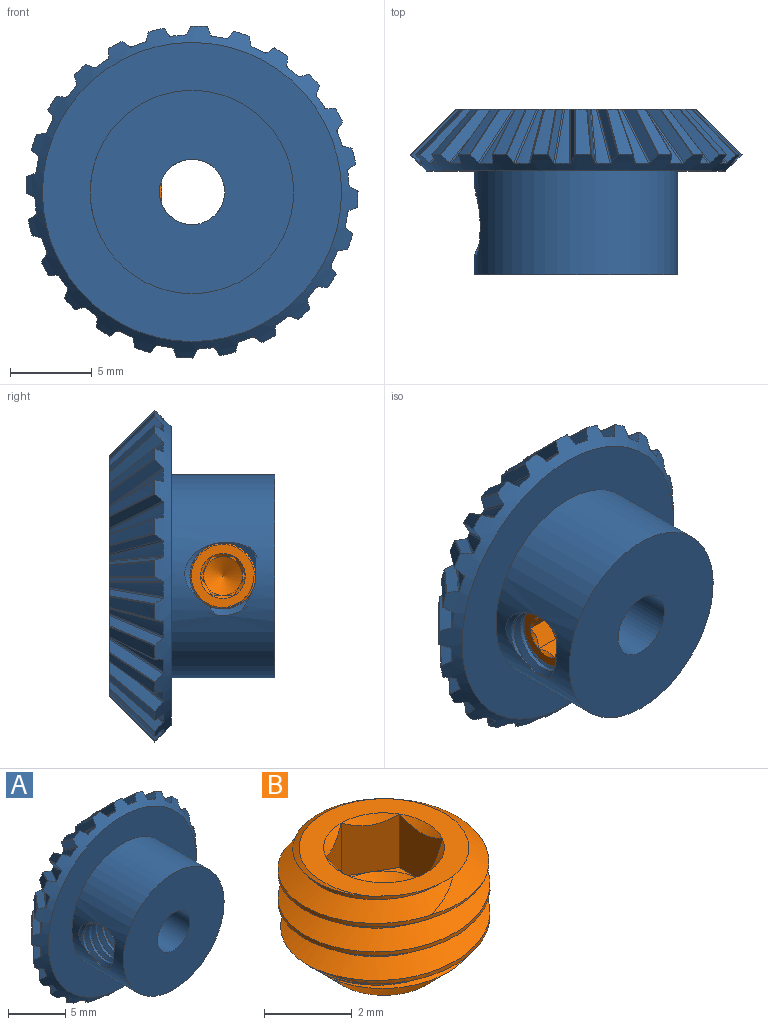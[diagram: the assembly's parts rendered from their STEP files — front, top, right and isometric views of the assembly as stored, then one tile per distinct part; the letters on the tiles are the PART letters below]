
ASSEMBLY  parts=2 mates=1
PART A: 224 faces, bbox 20.3x10.2x20.3 mm
  f0: cylinder r=2.41mm len=4.83mm, axis (-1,0,0), area 8.2mm2, adj f8,f9,f220,f221,f222,f223
  f1: cylinder r=2.41mm len=3.92mm, axis (-1,0,0), area 0.4mm2, adj f8,f218,f219
  f2: cylinder r=2.41mm len=2.98mm, axis (-1,0,0), area 0.3mm2, adj f8,f212,f213,f214
  f3: cone r=10.16mm half-angle=45deg, axis (0,-1,0), area 3.1mm2, adj f4,f14,f15,f18
  f4: cone r=10.16mm half-angle=45deg, axis (0,1,0), area 61.8mm2, adj f3,f13,f15,f16,f17,f18,f19,f20
  f5: cylinder r=2.02mm len=0.81mm, axis (-1,0,0), area 0.2mm2, adj f8,f208,f213
  f6: cylinder r=2.02mm len=4.59mm, axis (-1,0,0), area 16.9mm2, adj f8,f9,f218,f220,f222
  f7: cylinder r=2.02mm len=2.26mm, axis (-1,0,0), area 0.5mm2, adj f8,f212,f219
  f8: cylinder r=2mm len=10.13mm, axis (0,-1,0), area 107.9mm2, adj f0,f1,f2,f5,f6,f7,f10,f11
  f9: cylinder r=6.22mm len=12.45mm, axis (0,1,0), area 233.2mm2, adj f0,f6,f12,f13,f206,f220,f221,f222
  f10: cylinder r=2.02mm len=1.49mm, axis (-1,0,0), area 0.3mm2, adj f8,f211,f216
  f11: cylinder r=2.02mm len=3.04mm, axis (-1,0,0), area 0.7mm2, adj f8,f215,f223
  f12: cylinder r=2.02mm len=1.27mm, axis (-1,0,0), area 0mm2, adj f9,f221
  f13: plane 18.31x18.31mm, normal (0,-1,0), area 141.7mm2, adj f4,f9
  f14: plane 14.79x14.79mm, normal (0,1,0), area 137.6mm2, adj f3,f8,f15,f16,f17,f18,f19,f20
  f15: cylinder r=0.05mm len=2.83mm, axis (0,-0.71,-0.71), area 0.2mm2, adj f3,f4,f14,f16
  f16: plane 3.76x3.28mm, normal (0.94,0.24,-0.24), area 3.1mm2, adj f4,f14,f15,f17
  f17: cylinder r=0.1mm len=3.37mm, axis (0,-0.71,-0.71), area 0.6mm2, adj f4,f14,f16,f19
  f18: cylinder r=0.05mm len=2.83mm, axis (0.06,0.71,0.7), area 0.2mm2, adj f3,f4,f14,f20
  f19: cone r=5.83mm half-angle=45deg, axis (0,-1,0), area 2.7mm2, adj f4,f14,f17,f21
  f20: plane 3.77x3.28mm, normal (-0.96,0.24,-0.16), area 3.1mm2, adj f4,f14,f18,f22
  f21: cylinder r=0.1mm len=3.37mm, axis (-0.12,0.71,0.7), area 0.6mm2, adj f4,f14,f19,f23
  f22: cylinder r=0.1mm len=3.37mm, axis (0.06,0.71,0.7), area 0.6mm2, adj f4,f14,f20,f24
  f23: plane 3.66x3.28mm, normal (-0.88,0.24,-0.4), area 3.1mm2, adj f4,f14,f21,f25
  f24: cone r=5.83mm half-angle=45deg, axis (0,-1,0), area 2.7mm2, adj f4,f14,f22,f26
  f25: cylinder r=0.05mm len=2.83mm, axis (-0.12,0.71,0.7), area 0.2mm2, adj f4,f14,f23,f27
  f26: cylinder r=0.1mm len=3.37mm, axis (-0.18,-0.71,-0.68), area 0.6mm2, adj f4,f14,f24,f28
  f27: cone r=10.16mm half-angle=45deg, axis (0,-1,0), area 3.1mm2, adj f4,f14,f25,f29
  f28: plane 3.57x3.28mm, normal (0.85,0.24,-0.48), area 3.1mm2, adj f4,f14,f26,f30
  f29: cylinder r=0.05mm len=2.83mm, axis (0.18,-0.71,-0.68), area 0.2mm2, adj f4,f14,f27,f31
  f30: cylinder r=0.05mm len=2.83mm, axis (-0.18,-0.71,-0.68), area 0.2mm2, adj f4,f14,f28,f32
  f31: plane 3.69x3.28mm, normal (0.97,0.24,0.01), area 3.1mm2, adj f4,f14,f29,f33
  f32: cone r=10.16mm half-angle=45deg, axis (0,-1,0), area 3.1mm2, adj f4,f14,f30,f34
  f33: cylinder r=0.1mm len=3.37mm, axis (0.18,-0.71,-0.68), area 0.6mm2, adj f4,f14,f31,f35
  f34: cylinder r=0.05mm len=2.83mm, axis (0.24,0.71,0.66), area 0.2mm2, adj f4,f14,f32,f36
  f35: cone r=5.83mm half-angle=45deg, axis (0,-1,0), area 2.7mm2, adj f4,f14,f33,f37
  f36: plane 3.62x3.28mm, normal (-0.97,0.24,0.09), area 3.1mm2, adj f4,f14,f34,f38
  f37: cylinder r=0.1mm len=3.37mm, axis (-0.3,0.71,0.64), area 0.6mm2, adj f4,f14,f35,f39
  f38: cylinder r=0.1mm len=3.37mm, axis (0.24,0.71,0.66), area 0.6mm2, adj f4,f14,f36,f40
  f39: plane 3.3x3.28mm, normal (-0.75,0.24,-0.62), area 3.1mm2, adj f4,f14,f37,f41
  f40: cone r=5.83mm half-angle=45deg, axis (0,-1,0), area 2.7mm2, adj f4,f14,f38,f42
  f41: cylinder r=0.05mm len=2.83mm, axis (-0.3,0.71,0.64), area 0.2mm2, adj f4,f14,f39,f43
  f42: cylinder r=0.1mm len=3.37mm, axis (-0.35,-0.71,-0.61), area 0.6mm2, adj f4,f14,f40,f44
  f43: cone r=10.16mm half-angle=45deg, axis (0,-1,0), area 3.1mm2, adj f4,f14,f41,f45
  f44: plane 3.28x3.13mm, normal (0.69,0.24,-0.68), area 3.1mm2, adj f4,f14,f42,f46
  f45: cylinder r=0.05mm len=2.83mm, axis (0.35,-0.71,-0.61), area 0.2mm2, adj f4,f14,f43,f47
  f46: cylinder r=0.05mm len=2.83mm, axis (-0.35,-0.71,-0.61), area 0.2mm2, adj f4,f14,f44,f48
  f47: plane 3.38x3.28mm, normal (0.93,0.24,0.26), area 3.1mm2, adj f4,f14,f45,f49
  f48: cone r=10.16mm half-angle=45deg, axis (0,-1,0), area 3.1mm2, adj f4,f14,f46,f50
  f49: cylinder r=0.1mm len=3.37mm, axis (0.35,-0.71,-0.61), area 0.6mm2, adj f4,f14,f47,f51
  f50: cylinder r=0.05mm len=2.83mm, axis (0.41,0.71,0.58), area 0.2mm2, adj f4,f14,f48,f52
  f51: cone r=5.83mm half-angle=45deg, axis (0,-1,0), area 2.7mm2, adj f4,f14,f49,f53
  f52: plane 3.28x3.22mm, normal (-0.91,0.24,0.34), area 3.1mm2, adj f4,f14,f50,f54
  f53: cylinder r=0.1mm len=3.37mm, axis (-0.45,0.71,0.54), area 0.6mm2, adj f4,f14,f51,f55
  f54: cylinder r=0.1mm len=3.37mm, axis (0.41,0.71,0.58), area 0.6mm2, adj f4,f14,f52,f56
  f55: plane 3.28x2.72mm, normal (-0.56,0.24,-0.79), area 3.1mm2, adj f4,f14,f53,f57
  f56: cone r=5.83mm half-angle=45deg, axis (0,-1,0), area 2.7mm2, adj f4,f14,f54,f58
  f57: cylinder r=0.05mm len=2.83mm, axis (-0.45,0.71,0.54), area 0.2mm2, adj f4,f14,f55,f59
  f58: cylinder r=0.1mm len=3.37mm, axis (-0.5,-0.71,-0.5), area 0.6mm2, adj f4,f14,f56,f60
  f59: cone r=10.16mm half-angle=45deg, axis (0,-1,0), area 3.1mm2, adj f4,f14,f57,f61
  f60: plane 3.28x2.83mm, normal (0.49,0.24,-0.84), area 3.1mm2, adj f4,f14,f58,f62
  f61: cylinder r=0.05mm len=2.83mm, axis (0.5,-0.71,-0.5), area 0.2mm2, adj f4,f14,f59,f63
  f62: cylinder r=0.05mm len=2.83mm, axis (-0.5,-0.71,-0.5), area 0.2mm2, adj f4,f14,f60,f64
  f63: plane 3.28x2.83mm, normal (0.84,0.24,0.49), area 3.1mm2, adj f4,f14,f61,f65
  f64: cone r=10.16mm half-angle=45deg, axis (0,-1,0), area 3.1mm2, adj f4,f14,f62,f66
  f65: cylinder r=0.1mm len=3.37mm, axis (0.5,-0.71,-0.5), area 0.6mm2, adj f4,f14,f63,f67
  f66: cylinder r=0.05mm len=2.83mm, axis (0.54,0.71,0.45), area 0.2mm2, adj f4,f14,f64,f68
  f67: cone r=5.83mm half-angle=45deg, axis (0,-1,0), area 2.7mm2, adj f4,f14,f65,f69
  f68: plane 3.28x2.72mm, normal (-0.79,0.24,0.56), area 3.1mm2, adj f4,f14,f66,f70
  f69: cylinder r=0.1mm len=3.37mm, axis (-0.58,0.71,0.41), area 0.6mm2, adj f4,f14,f67,f71
  f70: cylinder r=0.1mm len=3.37mm, axis (0.54,0.71,0.45), area 0.6mm2, adj f4,f14,f68,f72
  f71: plane 3.28x3.22mm, normal (-0.34,0.24,-0.91), area 3.1mm2, adj f4,f14,f69,f73
  f72: cone r=5.83mm half-angle=45deg, axis (0,-1,0), area 2.7mm2, adj f4,f14,f70,f74
  f73: cylinder r=0.05mm len=2.83mm, axis (-0.58,0.71,0.41), area 0.2mm2, adj f4,f14,f71,f75
  f74: cylinder r=0.1mm len=3.37mm, axis (-0.61,-0.71,-0.35), area 0.6mm2, adj f4,f14,f72,f76
  f75: cone r=10.16mm half-angle=45deg, axis (0,-1,0), area 3.1mm2, adj f4,f14,f73,f77
  f76: plane 3.38x3.28mm, normal (0.26,0.24,-0.93), area 3.1mm2, adj f4,f14,f74,f78
  f77: cylinder r=0.05mm len=2.83mm, axis (0.61,-0.71,-0.35), area 0.2mm2, adj f4,f14,f75,f79
  f78: cylinder r=0.05mm len=2.83mm, axis (-0.61,-0.71,-0.35), area 0.2mm2, adj f4,f14,f76,f80
  f79: plane 3.28x3.13mm, normal (0.68,0.24,0.69), area 3.1mm2, adj f4,f14,f77,f81
  f80: cone r=10.16mm half-angle=45deg, axis (0,-1,0), area 3.1mm2, adj f4,f14,f78,f82
  f81: cylinder r=0.1mm len=3.37mm, axis (0.61,-0.71,-0.35), area 0.6mm2, adj f4,f14,f79,f83
  f82: cylinder r=0.05mm len=2.83mm, axis (0.64,0.71,0.3), area 0.2mm2, adj f4,f14,f80,f84
  f83: cone r=5.83mm half-angle=45deg, axis (0,-1,0), area 2.7mm2, adj f4,f14,f81,f85
  f84: plane 3.3x3.28mm, normal (-0.62,0.24,0.75), area 3.1mm2, adj f4,f14,f82,f86
  f85: cylinder r=0.1mm len=3.37mm, axis (-0.66,0.71,0.24), area 0.6mm2, adj f4,f14,f83,f87
  f86: cylinder r=0.1mm len=3.37mm, axis (0.64,0.71,0.3), area 0.6mm2, adj f4,f14,f84,f88
  f87: plane 3.62x3.28mm, normal (-0.09,0.24,-0.97), area 3.1mm2, adj f4,f14,f85,f89
  f88: cone r=5.83mm half-angle=45deg, axis (0,-1,0), area 2.7mm2, adj f4,f14,f86,f90
  f89: cylinder r=0.05mm len=2.83mm, axis (-0.66,0.71,0.24), area 0.2mm2, adj f4,f14,f87,f91
  f90: cylinder r=0.1mm len=3.37mm, axis (-0.68,-0.71,-0.18), area 0.6mm2, adj f4,f14,f88,f92
  f91: cone r=10.16mm half-angle=45deg, axis (0,-1,0), area 3.1mm2, adj f4,f14,f89,f93
  f92: plane 3.69x3.28mm, normal (0.01,0.24,-0.97), area 3.1mm2, adj f4,f14,f90,f94
  f93: cylinder r=0.05mm len=2.83mm, axis (0.68,-0.71,-0.18), area 0.2mm2, adj f4,f14,f91,f95
  f94: cylinder r=0.05mm len=2.83mm, axis (-0.68,-0.71,-0.18), area 0.2mm2, adj f4,f14,f92,f96
  f95: plane 3.57x3.28mm, normal (0.48,0.24,0.85), area 3.1mm2, adj f4,f14,f93,f97
  f96: cone r=10.16mm half-angle=45deg, axis (0,-1,0), area 3.1mm2, adj f4,f14,f94,f98
  f97: cylinder r=0.1mm len=3.37mm, axis (0.68,-0.71,-0.18), area 0.6mm2, adj f4,f14,f95,f99
  f98: cylinder r=0.05mm len=2.83mm, axis (0.7,0.71,0.12), area 0.2mm2, adj f4,f14,f96,f100
  f99: cone r=5.83mm half-angle=45deg, axis (0,-1,0), area 2.7mm2, adj f4,f14,f97,f101
  f100: plane 3.66x3.28mm, normal (-0.4,0.24,0.88), area 3.1mm2, adj f4,f14,f98,f102
  f101: cylinder r=0.1mm len=3.37mm, axis (-0.7,0.71,0.06), area 0.6mm2, adj f4,f14,f99,f103
  f102: cylinder r=0.1mm len=3.37mm, axis (0.7,0.71,0.12), area 0.6mm2, adj f4,f14,f100,f104
  f103: plane 3.77x3.28mm, normal (0.16,0.24,-0.96), area 3.1mm2, adj f4,f14,f101,f105
  f104: cone r=5.83mm half-angle=45deg, axis (0,-1,0), area 2.7mm2, adj f4,f14,f102,f106
  f105: cylinder r=0.05mm len=2.83mm, axis (-0.7,0.71,0.06), area 0.2mm2, adj f4,f14,f103,f107
  f106: cylinder r=0.1mm len=3.37mm, axis (-0.71,-0.71,0), area 0.6mm2, adj f4,f14,f104,f108
  f107: cone r=10.16mm half-angle=45deg, axis (0,-1,0), area 3.1mm2, adj f4,f14,f105,f109
  f108: plane 3.76x3.28mm, normal (-0.24,0.24,-0.94), area 3.1mm2, adj f4,f14,f106,f110
  f109: cylinder r=0.05mm len=2.83mm, axis (0.71,-0.71,0), area 0.2mm2, adj f4,f14,f107,f111
  f110: cylinder r=0.05mm len=2.83mm, axis (-0.71,-0.71,0), area 0.2mm2, adj f4,f14,f108,f112
  f111: plane 3.76x3.28mm, normal (0.24,0.24,0.94), area 3.1mm2, adj f4,f14,f109,f113
  f112: cone r=10.16mm half-angle=45deg, axis (0,-1,0), area 3.1mm2, adj f4,f14,f110,f114
  f113: cylinder r=0.1mm len=3.37mm, axis (0.71,-0.71,0), area 0.6mm2, adj f4,f14,f111,f115
  f114: cylinder r=0.05mm len=2.83mm, axis (0.7,0.71,-0.06), area 0.2mm2, adj f4,f14,f112,f116
  f115: cone r=5.83mm half-angle=45deg, axis (0,-1,0), area 2.7mm2, adj f4,f14,f113,f117
  f116: plane 3.77x3.28mm, normal (-0.16,0.24,0.96), area 3.1mm2, adj f4,f14,f114,f118
  f117: cylinder r=0.1mm len=3.37mm, axis (-0.7,0.71,-0.12), area 0.6mm2, adj f4,f14,f115,f119
  f118: cylinder r=0.1mm len=3.37mm, axis (0.7,0.71,-0.06), area 0.6mm2, adj f4,f14,f116,f120
  f119: plane 3.66x3.28mm, normal (0.4,0.24,-0.88), area 3.1mm2, adj f4,f14,f117,f121
  f120: cone r=5.83mm half-angle=45deg, axis (0,-1,0), area 2.7mm2, adj f4,f14,f118,f122
  f121: cylinder r=0.05mm len=2.83mm, axis (-0.7,0.71,-0.12), area 0.2mm2, adj f4,f14,f119,f123
  f122: cylinder r=0.1mm len=3.37mm, axis (-0.68,-0.71,0.18), area 0.6mm2, adj f4,f14,f120,f124
  f123: cone r=10.16mm half-angle=45deg, axis (0,-1,0), area 3.1mm2, adj f4,f14,f121,f125
  f124: plane 3.57x3.28mm, normal (-0.48,0.24,-0.85), area 3.1mm2, adj f4,f14,f122,f126
  f125: cylinder r=0.05mm len=2.83mm, axis (0.68,-0.71,0.18), area 0.2mm2, adj f4,f14,f123,f127
  f126: cylinder r=0.05mm len=2.83mm, axis (-0.68,-0.71,0.18), area 0.2mm2, adj f4,f14,f124,f128
  f127: plane 3.69x3.28mm, normal (-0.01,0.24,0.97), area 3.1mm2, adj f4,f14,f125,f129
  f128: cone r=10.16mm half-angle=45deg, axis (0,-1,0), area 3.1mm2, adj f4,f14,f126,f130
  f129: cylinder r=0.1mm len=3.37mm, axis (0.68,-0.71,0.18), area 0.6mm2, adj f4,f14,f127,f131
  f130: cylinder r=0.05mm len=2.83mm, axis (0.66,0.71,-0.24), area 0.2mm2, adj f4,f14,f128,f132
  f131: cone r=5.83mm half-angle=45deg, axis (0,-1,0), area 2.7mm2, adj f4,f14,f129,f133
  f132: plane 3.62x3.28mm, normal (0.09,0.24,0.97), area 3.1mm2, adj f4,f14,f130,f134
  f133: cylinder r=0.1mm len=3.37mm, axis (-0.64,0.71,-0.3), area 0.6mm2, adj f4,f14,f131,f135
  f134: cylinder r=0.1mm len=3.37mm, axis (0.66,0.71,-0.24), area 0.6mm2, adj f4,f14,f132,f136
  f135: plane 3.3x3.28mm, normal (0.62,0.24,-0.75), area 3.1mm2, adj f4,f14,f133,f137
  f136: cone r=5.83mm half-angle=45deg, axis (0,-1,0), area 2.7mm2, adj f4,f14,f134,f138
  f137: cylinder r=0.05mm len=2.83mm, axis (-0.64,0.71,-0.3), area 0.2mm2, adj f4,f14,f135,f139
  f138: cylinder r=0.1mm len=3.37mm, axis (-0.61,-0.71,0.35), area 0.6mm2, adj f4,f14,f136,f140
  f139: cone r=10.16mm half-angle=45deg, axis (0,-1,0), area 3.1mm2, adj f4,f14,f137,f141
  f140: plane 3.28x3.13mm, normal (-0.68,0.24,-0.69), area 3.1mm2, adj f4,f14,f138,f142
  f141: cylinder r=0.05mm len=2.83mm, axis (0.61,-0.71,0.35), area 0.2mm2, adj f4,f14,f139,f143
  f142: cylinder r=0.05mm len=2.83mm, axis (-0.61,-0.71,0.35), area 0.2mm2, adj f4,f14,f140,f144
  f143: plane 3.38x3.28mm, normal (-0.26,0.24,0.93), area 3.1mm2, adj f4,f14,f141,f145
  f144: cone r=10.16mm half-angle=45deg, axis (0,-1,0), area 3.1mm2, adj f4,f14,f142,f146
  f145: cylinder r=0.1mm len=3.37mm, axis (0.61,-0.71,0.35), area 0.6mm2, adj f4,f14,f143,f147
  f146: cylinder r=0.05mm len=2.83mm, axis (0.58,0.71,-0.41), area 0.2mm2, adj f4,f14,f144,f148
  f147: cone r=5.83mm half-angle=45deg, axis (0,-1,0), area 2.7mm2, adj f4,f14,f145,f149
  f148: plane 3.28x3.22mm, normal (0.34,0.24,0.91), area 3.1mm2, adj f4,f14,f146,f150
  f149: cylinder r=0.1mm len=3.37mm, axis (-0.54,0.71,-0.45), area 0.6mm2, adj f4,f14,f147,f151
  f150: cylinder r=0.1mm len=3.37mm, axis (0.58,0.71,-0.41), area 0.6mm2, adj f4,f14,f148,f152
  f151: plane 3.28x2.72mm, normal (0.79,0.24,-0.56), area 3.1mm2, adj f4,f14,f149,f153
  f152: cone r=5.83mm half-angle=45deg, axis (0,-1,0), area 2.7mm2, adj f4,f14,f150,f154
  f153: cylinder r=0.05mm len=2.83mm, axis (-0.54,0.71,-0.45), area 0.2mm2, adj f4,f14,f151,f155
  f154: cylinder r=0.1mm len=3.37mm, axis (-0.5,-0.71,0.5), area 0.6mm2, adj f4,f14,f152,f156
  f155: cone r=10.16mm half-angle=45deg, axis (0,-1,0), area 3.1mm2, adj f4,f14,f153,f157
  f156: plane 3.28x2.83mm, normal (-0.84,0.24,-0.49), area 3.1mm2, adj f4,f14,f154,f158
  f157: cylinder r=0.05mm len=2.83mm, axis (0.5,-0.71,0.5), area 0.2mm2, adj f4,f14,f155,f159
  f158: cylinder r=0.05mm len=2.83mm, axis (-0.5,-0.71,0.5), area 0.2mm2, adj f4,f14,f156,f160
  f159: plane 3.28x2.83mm, normal (-0.49,0.24,0.84), area 3.1mm2, adj f4,f14,f157,f161
  f160: cone r=10.16mm half-angle=45deg, axis (0,-1,0), area 3.1mm2, adj f4,f14,f158,f162
  f161: cylinder r=0.1mm len=3.37mm, axis (0.5,-0.71,0.5), area 0.6mm2, adj f4,f14,f159,f163
  f162: cylinder r=0.05mm len=2.83mm, axis (0.45,0.71,-0.54), area 0.2mm2, adj f4,f14,f160,f164
  f163: cone r=5.83mm half-angle=45deg, axis (0,-1,0), area 2.7mm2, adj f4,f14,f161,f165
  f164: plane 3.28x2.72mm, normal (0.56,0.24,0.79), area 3.1mm2, adj f4,f14,f162,f166
  f165: cylinder r=0.1mm len=3.37mm, axis (-0.41,0.71,-0.58), area 0.6mm2, adj f4,f14,f163,f167
  f166: cylinder r=0.1mm len=3.37mm, axis (0.45,0.71,-0.54), area 0.6mm2, adj f4,f14,f164,f168
  f167: plane 3.28x3.22mm, normal (0.91,0.24,-0.34), area 3.1mm2, adj f4,f14,f165,f169
  f168: cone r=5.83mm half-angle=45deg, axis (0,-1,0), area 2.7mm2, adj f4,f14,f166,f170
  f169: cylinder r=0.05mm len=2.83mm, axis (-0.41,0.71,-0.58), area 0.2mm2, adj f4,f14,f167,f171
  f170: cylinder r=0.1mm len=3.37mm, axis (-0.35,-0.71,0.61), area 0.6mm2, adj f4,f14,f168,f172
  f171: cone r=10.16mm half-angle=45deg, axis (0,-1,0), area 3.1mm2, adj f4,f14,f169,f173
  f172: plane 3.38x3.28mm, normal (-0.93,0.24,-0.26), area 3.1mm2, adj f4,f14,f170,f174
  f173: cylinder r=0.05mm len=2.83mm, axis (0.35,-0.71,0.61), area 0.2mm2, adj f4,f14,f171,f175
  f174: cylinder r=0.05mm len=2.83mm, axis (-0.35,-0.71,0.61), area 0.2mm2, adj f4,f14,f172,f176
  f175: plane 3.28x3.13mm, normal (-0.69,0.24,0.68), area 3.1mm2, adj f4,f14,f173,f177
  f176: cone r=10.16mm half-angle=45deg, axis (0,-1,0), area 3.1mm2, adj f4,f14,f174,f178
  f177: cylinder r=0.1mm len=3.37mm, axis (0.35,-0.71,0.61), area 0.6mm2, adj f4,f14,f175,f179
  f178: cylinder r=0.05mm len=2.83mm, axis (0.3,0.71,-0.64), area 0.2mm2, adj f4,f14,f176,f180
  f179: cone r=5.83mm half-angle=45deg, axis (0,-1,0), area 2.7mm2, adj f4,f14,f177,f181
  f180: plane 3.3x3.28mm, normal (0.75,0.24,0.62), area 3.1mm2, adj f4,f14,f178,f182
  f181: cylinder r=0.1mm len=3.37mm, axis (-0.24,0.71,-0.66), area 0.6mm2, adj f4,f14,f179,f183
  f182: cylinder r=0.1mm len=3.37mm, axis (0.3,0.71,-0.64), area 0.6mm2, adj f4,f14,f180,f184
  f183: plane 3.62x3.28mm, normal (0.97,0.24,-0.09), area 3.1mm2, adj f4,f14,f181,f185
  f184: cone r=5.83mm half-angle=45deg, axis (0,-1,0), area 2.7mm2, adj f4,f14,f182,f186
  f185: cylinder r=0.05mm len=2.83mm, axis (-0.24,0.71,-0.66), area 0.2mm2, adj f4,f14,f183,f187
  f186: cylinder r=0.1mm len=3.37mm, axis (-0.18,-0.71,0.68), area 0.6mm2, adj f4,f14,f184,f188
  f187: cone r=10.16mm half-angle=45deg, axis (0,-1,0), area 3.1mm2, adj f4,f14,f185,f189
  f188: plane 3.69x3.28mm, normal (-0.97,0.24,-0.01), area 3.1mm2, adj f4,f14,f186,f190
  f189: cylinder r=0.05mm len=2.83mm, axis (0.18,-0.71,0.68), area 0.2mm2, adj f4,f14,f187,f191
  f190: cylinder r=0.05mm len=2.83mm, axis (-0.18,-0.71,0.68), area 0.2mm2, adj f4,f14,f188,f192
  f191: plane 3.57x3.28mm, normal (-0.85,0.24,0.48), area 3.1mm2, adj f4,f14,f189,f193
  f192: cone r=10.16mm half-angle=45deg, axis (0,-1,0), area 3.1mm2, adj f4,f14,f190,f194
  f193: cylinder r=0.1mm len=3.37mm, axis (0.18,-0.71,0.68), area 0.6mm2, adj f4,f14,f191,f195
  f194: cylinder r=0.05mm len=2.83mm, axis (0.12,0.71,-0.7), area 0.2mm2, adj f4,f14,f192,f196
  f195: cone r=5.83mm half-angle=45deg, axis (0,-1,0), area 2.7mm2, adj f4,f14,f193,f197
  f196: plane 3.66x3.28mm, normal (0.88,0.24,0.4), area 3.1mm2, adj f4,f14,f194,f198
  f197: cylinder r=0.1mm len=3.37mm, axis (-0.06,0.71,-0.7), area 0.6mm2, adj f4,f14,f195,f199
  f198: cylinder r=0.1mm len=3.37mm, axis (0.12,0.71,-0.7), area 0.6mm2, adj f4,f14,f196,f200
  f199: plane 3.77x3.28mm, normal (0.96,0.24,0.16), area 3.1mm2, adj f4,f14,f197,f201
  f200: cone r=5.83mm half-angle=45deg, axis (0,-1,0), area 2.7mm2, adj f4,f14,f198,f202
  f201: cylinder r=0.05mm len=2.83mm, axis (-0.06,0.71,-0.7), area 0.2mm2, adj f4,f14,f199,f203
  f202: cylinder r=0.1mm len=3.37mm, axis (0,-0.71,0.71), area 0.6mm2, adj f4,f14,f200,f204
  f203: cone r=10.16mm half-angle=45deg, axis (0,-1,0), area 3.1mm2, adj f4,f14,f201,f205
  f204: plane 3.76x3.28mm, normal (-0.94,0.24,0.24), area 3.1mm2, adj f4,f14,f202,f205
  f205: cylinder r=0.05mm len=2.83mm, axis (0,-0.71,0.71), area 0.2mm2, adj f4,f14,f203,f204
  f206: plane 12.45x12.45mm, normal (0,-1,0), area 109.1mm2, adj f8,f9
  f207: cylinder r=2.02mm len=0.61mm, axis (-1,0,0), area 0.1mm2, adj f8,f209,f210
  f208: plane 0.56x0.02mm, normal (-1,0,0), area 0mm2, adj f5,f8
  f209: plane 0.56x0.02mm, normal (-1,0,0), area 0mm2, adj f8,f207
  f210: cone r=5.07mm half-angle=45deg, axis (-1,0,0), area 0.4mm2, adj f8,f207,f211
  f211: bspline ~2.54x0.93mm, area 0.4mm2, adj f8,f10,f210
  f212: bspline ~2.98x0.85mm, area 1.1mm2, adj f2,f7,f8
  f213: bspline ~2.69x0.82mm, area 0.8mm2, adj f2,f5,f8,f214
  f214: cone r=5.07mm half-angle=45deg, axis (-1,0,0), area 0.1mm2, adj f2,f8,f213
  f215: bspline ~3.92x1.62mm, area 1.5mm2, adj f8,f11,f217
  f216: bspline ~3.27x0.97mm, area 1.1mm2, adj f8,f10,f217
  f217: cylinder r=2.41mm len=3.39mm, axis (-1,0,0), area 0.4mm2, adj f8,f215,f216
  f218: bspline ~4.03x1.5mm, area 2mm2, adj f1,f6,f8
  f219: bspline ~3.78x1.25mm, area 1.5mm2, adj f1,f7,f8
  f220: bspline ~4.81x4.81mm, area 32.5mm2, adj f0,f6,f8,f9
  f221: bspline ~3.58x1.5mm, area 1.2mm2, adj f0,f9,f12
  f222: bspline ~4.82x4.82mm, area 33.6mm2, adj f0,f6,f8,f9
  f223: bspline ~4.72x2.64mm, area 2mm2, adj f0,f8,f11
PART B: 27 faces, bbox 5.3x5.3x4 mm
  f0: cone r=1.19mm half-angle=60deg, axis (0,0,1), area 5.1mm2, adj f1,f22,f23,f24,f25,f26
  f1: plane 1.03x0.6mm, normal (0,0,1), area 0.1mm2, adj f0,f2,f21
  f2: plane 2.01x1.71mm, normal (-0.5,0.87,0), area 1.9mm2, adj f1,f3,f20,f21,f26
  f3: cone r=1.37mm half-angle=45deg, axis (0,0,1), area 0mm2, adj f2,f4
  f4: plane 4.31x4.29mm, normal (0,0,1), area 5.7mm2, adj f3,f5,f9,f10,f11,f12,f13,f17
  f5: cone r=1.37mm half-angle=45deg, axis (0,0,1), area 0mm2, adj f4,f6
  f6: plane 2.01x1.9mm, normal (1,0,0), area 1.9mm2, adj f5,f7,f20,f24,f25
  f7: plane 2.01x1.71mm, normal (0.5,-0.87,0), area 1.9mm2, adj f6,f8,f12,f23,f24
  f8: plane 2.01x1.71mm, normal (-0.5,-0.87,0), area 1.9mm2, adj f7,f11,f21,f22,f23
  f9: cone r=1.37mm half-angle=45deg, axis (0,0,1), area 0mm2, adj f4,f20
  f10: cone r=1.37mm half-angle=45deg, axis (0,0,1), area 0.2mm2, adj f4,f21
  f11: cone r=1.37mm half-angle=45deg, axis (0,0,1), area 0mm2, adj f4,f8
  f12: cone r=1.37mm half-angle=45deg, axis (0,0,1), area 0mm2, adj f4,f7
  f13: cylinder r=1.9mm len=3.8mm, axis (0,0,1), area 3.9mm2, adj f4,f14,f17,f19
  f14: cone r=1.32mm half-angle=45deg, axis (0,0,1), area 13mm2, adj f13,f15,f16,f17,f19
  f15: cylinder r=2.41mm len=4.83mm, axis (0,0,1), area 3.3mm2, adj f14,f17,f18,f19
  f16: cone r=1664.28mm half-angle=59deg, axis (0,0,-1), area 6.4mm2, adj f14
  f17: bspline ~4.81x4.79mm, area 22mm2, adj f4,f13,f14,f15,f18
  f18: cone r=2.41mm half-angle=55deg, axis (0,0,-1), area 3.7mm2, adj f4,f15,f17,f19
  f19: bspline ~4.83x4.83mm, area 22.4mm2, adj f4,f13,f14,f15,f18
  f20: plane 2.01x1.71mm, normal (0.5,0.87,0), area 1.9mm2, adj f2,f6,f9,f25,f26
  f21: plane 1.62x1.51mm, normal (-1,0,0), area 1.9mm2, adj f1,f2,f8,f10,f22
  f22: plane 1.03x0.6mm, normal (0,0,1), area 0.1mm2, adj f0,f8,f21
  f23: plane 1.19x0.34mm, normal (0,0,1), area 0.1mm2, adj f0,f7,f8
  f24: plane 1.03x0.6mm, normal (0,0,1), area 0.1mm2, adj f0,f6,f7
  f25: plane 1.03x0.6mm, normal (0,0,1), area 0.1mm2, adj f0,f6,f20
  f26: plane 1.19x0.34mm, normal (0,0,1), area 0.1mm2, adj f0,f2,f20
PLACE A t=(0,4.97,0)mm
PLACE B rot(axis=(0,-1,0),90deg) t=(-3.85,3.18,0)mm
MATE fastened B.f15 <-> A.f0  axis (-1,0,0) through (-3.83,3.18,0)mm
